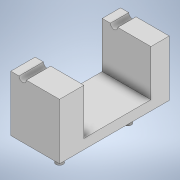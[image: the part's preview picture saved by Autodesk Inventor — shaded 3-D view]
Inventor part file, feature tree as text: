
AUTODESK INVENTOR PART (.ipt)
format: ipt  version: 2021 (Build 250183000, 183)  size: 132,608 bytes
history: native  units: mm
features: extrude x4, sketch x4
ambient origin geometry x8: Origin, YZ Plane, XZ Plane, XY Plane, X Axis, Y Axis, Z Axis, Center Point
bodies: Solid1 (feature_tree)
feature tree (8):
  extrude  "Extrusion1"  Depth=22.877mm
  extrude  "Extrusion2"  Depth=20.0mm TaperAngle=0.0deg
  extrude  "Extrusion3"  Depth=3.0mm
  extrude  "Extrusion4"  Depth=10.0mm
  sketch  "Sketch1"  dims[d0=45.0mm d1=22.877mm]
  sketch  "Sketch2"  dims[d2=11.4385mm d4=20.0mm d5=0.0mm]
  sketch  "Sketch3"  dims[d6=3.0mm d7=3.0mm]
  sketch  "Sketch4"  dims[d8=28.0mm d10=3.5mm d12=3.5mm d13=3.0mm d14=0.0mm d15=17.5mm d17=7.5mm d18=4.0mm d19=0.0mm d20=0.0mm d21=3.0mm d22=15.113mm d23=0.0mm d24=0.0mm d25=10.0mm]
